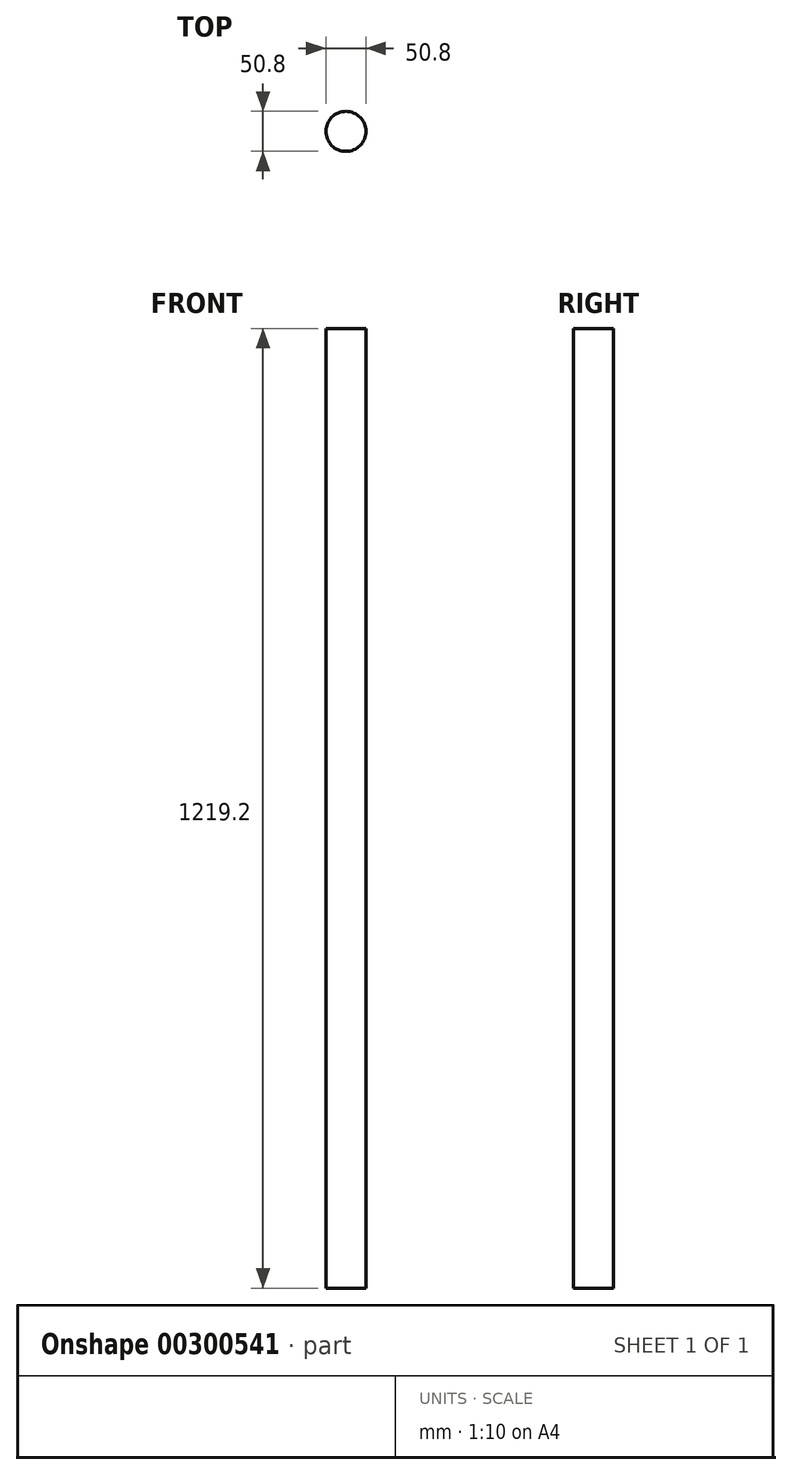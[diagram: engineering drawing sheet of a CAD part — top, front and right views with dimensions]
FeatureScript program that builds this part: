
annotation { "Feature Type Name" : "Feature", "Feature Type Description" : "" }
export const myFeature = defineFeature(function(context is Context, id is Id, definition is map)
    precondition{}
    {
        {
            var Q0;
            Q0=qCreatedBy(makeId("Front.planeOp"),FACE);
            var sketch = newSketch(context, id + "F0", { "sketchPlane" : qUnion([Q0])});
            skLineSegment(sketch, "E0", {"start": v(0, 1086.34) * mm, "end": v(0, -132.86) * mm});
            skLineSegment(sketch, "E1", {"start": v(0, -132.86) * mm, "end": v(25.4, -132.86) * mm});
            skLineSegment(sketch, "E2", {"start": v(25.4, -132.86) * mm, "end": v(25.4, 1086.34) * mm});
            skLineSegment(sketch, "E3", {"start": v(25.4, 1086.34) * mm, "end": v(0, 1086.34) * mm});
            skSolve(sketch);
        }
        {
            var Q0;
            Q0 = qSketchRegion(id + "F0", true);
            var Q1;
            Q1=sQuery(id+"F0.wireOp",EDGE,"E0");
            revolve(context, id + "F1", {"entities" : qUnion([Q0]), "axis" : qUnion([Q1]), "revolveType" : RevolveType.FULL});
        }
    });
